MODEL slx_5d9a9d625d33
KIND model
CONFIG AbsTol = auto
CONFIG EnableMultiTasking = off
CONFIG FixedStep = auto
CONFIG MaxStep = auto
CONFIG MinStep = auto
CONFIG RelTol = 1e-3
CONFIG SampleTimeConstraint = Unconstrained
CONFIG SolverName = VariableStepAuto
CONFIG StartTime = 0.0
CONFIG StopTime = 10.0
BLOCK [Sum] Add
  IconShape = rectangular
BLOCK [Sum] Add2
  IconShape = rectangular
BLOCK [Sum] Add3
  IconShape = rectangular
BLOCK [Reference] Counter2  REF=dspswit3/Counter
  SourceBlock = dspswit3/Counter
  SourceType = Counter
BLOCK [Product] Divide
  Inputs = */
BLOCK [Product] Divide1
  Inputs = */
BLOCK [Product] Divide3
  Inputs = */
BLOCK [Product] Divide4
  Inputs = */
BLOCK [Reference] LPF 1  REF=dsparch4/Analog
Filter Design
  SourceBlock = dsparch4/Analog\nFilter Design
  SourceType = Analog Filter Design
BLOCK [Reference] LPF 2  REF=dsparch4/Analog
Filter Design
  SourceBlock = dsparch4/Analog\nFilter Design
  SourceType = Analog Filter Design
BLOCK [Gain] Multiply1
  Gain = 2
BLOCK [Gain] Multiply2
  Gain = 2
BLOCK [Product] Product1
BLOCK [Product] Product2
BLOCK [Product] Product5
BLOCK [Product] Product6
BLOCK [Scope] Scope
  Floating = off
  NumInputPorts = 2
  ScopeSpecificationString = Simulink.scopes.TimeScopeBlockCfg('CurrentConfiguration', extmgr.ConfigurationSet(extmgr.Configuration('Core','General UI',true),extmgr.Configuration('Core','Source UI',true),extmgr.Configuration('Sources','WiredSimulink',true),extmgr.Configuration('Visuals','Time Domain',true,'SerializedDisplays',{struct('MinYLimReal','0.0068','MaxYLimReal','9.98352','YLabelReal','','MinYLimMag','0.0068','MaxYLim...<+2059ch>
BLOCK [Scope] Scope1
  Floating = off
  NumInputPorts = 2
  ScopeSpecificationString = Simulink.scopes.TimeScopeBlockCfg('CurrentConfiguration', extmgr.ConfigurationSet(extmgr.Configuration('Core','General UI',true),extmgr.Configuration('Core','Source UI',true),extmgr.Configuration('Sources','WiredSimulink',true,'DataLoggingVariableName','ScopeData1'),extmgr.Configuration('Visuals','Time Domain',true,'SerializedDisplays',{struct('MinYLimReal','-1.25','MaxYLimReal','1.25','YLabelReal...<+2117ch>
BLOCK [Scope] Scope2
  Floating = off
  NumInputPorts = 2
  ScopeSpecificationString = Simulink.scopes.TimeScopeBlockCfg('CurrentConfiguration', extmgr.ConfigurationSet(extmgr.Configuration('Core','General UI',true),extmgr.Configuration('Core','Source UI',true),extmgr.Configuration('Sources','WiredSimulink',true,'DataLoggingVariableName','ScopeData2'),extmgr.Configuration('Visuals','Time Domain',true,'SerializedDisplays',{struct('MinYLimReal','-0.13898','MaxYLimReal','1.25086','YLab...<+2101ch>
BLOCK [Sqrt] Sqrt1
BLOCK [Sqrt] Sqrt2
BLOCK [Math] Square1
  Operator = square
  SignedPower = on
BLOCK [Math] Square2
  Operator = square
  SignedPower = on
BLOCK [Math] Square5
  Operator = square
  SignedPower = on
BLOCK [Math] Square6
  Operator = square
  SignedPower = on
BLOCK [Sum] Sum3
  Inputs = |++
BLOCK [Sum] Sum6
  Inputs = |++
BLOCK [Trigonometry] Trigonometric Function
  Operator = atan
BLOCK [Trigonometry] Trigonometric Function1
  Operator = atan
BLOCK [UnitDelay] Unit Delay5
  HasFrameUpgradeWarning = on
  NameLocation = top
  SampleTime = -1
BLOCK [UnitDelay] Unit Delay6
  HasFrameUpgradeWarning = on
  NameLocation = top
  SampleTime = -1
BLOCK [Sin] cos ref
  Frequency = 50
  Phase = 0.5*pi
  SampleTime = 1/12000
BLOCK [RandomNumber] noise
  SampleTime = 1/12000
  Variance = 10
BLOCK [Sin] sin ref
  Frequency = 50
  SampleTime = 1/12000
BLOCK [Sin] target signal
  Frequency = 50
  Phase = 0.3*pi
  SampleTime = 1/12000
ANNOTATION (root): Quadrature vector type digital Lock- amplifier I provide two examples of LIA. The difference lies in how the DC component is extracted after the phase-sensitive detectors (PSDs). The first architecture filters the AC components by means of integral averaging, and the second architecture allows the user to simply adjust the cutoff frequency and other parameters of the low-pass filter. Meng Zhang: <...<+6ch>
ANNOTATION (root): LIA based on LPF module
ANNOTATION (root): LIA based on integral averaging module
ANNOTATION (root): constant relationship
ANNOTATION (root): input signal with noise
ANNOTATION (root): reference signals
LINE Add2:1 -> Sqrt2:1
LINE Add3:1 -> Sqrt1:1
NET Add:1 -> Product1:1, Product2:1, Product5:1, Product6:1, Scope1:2
NET Counter2:1 -> Divide3:2, Divide4:2
LINE Divide1:1 -> Trigonometric Function1:1
NET Divide3:1 -> Divide:2, Square5:1
NET Divide4:1 -> Divide:1, Square6:1
LINE Divide:1 -> Trigonometric Function:1
NET LPF 1:1 -> Divide1:2, Square1:1
NET LPF 2:1 -> Divide1:1, Square2:1
LINE Multiply1:1 -> Scope2:1
LINE Multiply2:1 -> Scope:1
LINE Product1:1 -> LPF 1:1
LINE Product2:1 -> LPF 2:1
LINE Product5:1 -> Sum3:1
LINE Product6:1 -> Sum6:1
LINE Sqrt1:1 -> Multiply1:1
LINE Sqrt2:1 -> Multiply2:1
LINE Square1:1 -> Add3:1
LINE Square2:1 -> Add3:2
LINE Square5:1 -> Add2:1
LINE Square6:1 -> Add2:2
NET Sum3:1 -> Divide3:1, Unit Delay5:1
NET Sum6:1 -> Divide4:1, Unit Delay6:1
LINE Trigonometric Function1:1 -> Scope2:2
LINE Trigonometric Function:1 -> Scope:2
LINE Unit Delay5:1 -> Sum3:2
LINE Unit Delay6:1 -> Sum6:2
NET cos ref:1 -> Product2:2, Product6:2
LINE noise:1 -> Add:2
NET sin ref:1 -> Product1:2, Product5:2
NET target signal:1 -> Add:1, Scope1:1
note: NET lines group one-source signal fan-out (src -> all destinations, sorted); 1:1 wires keep LINE
